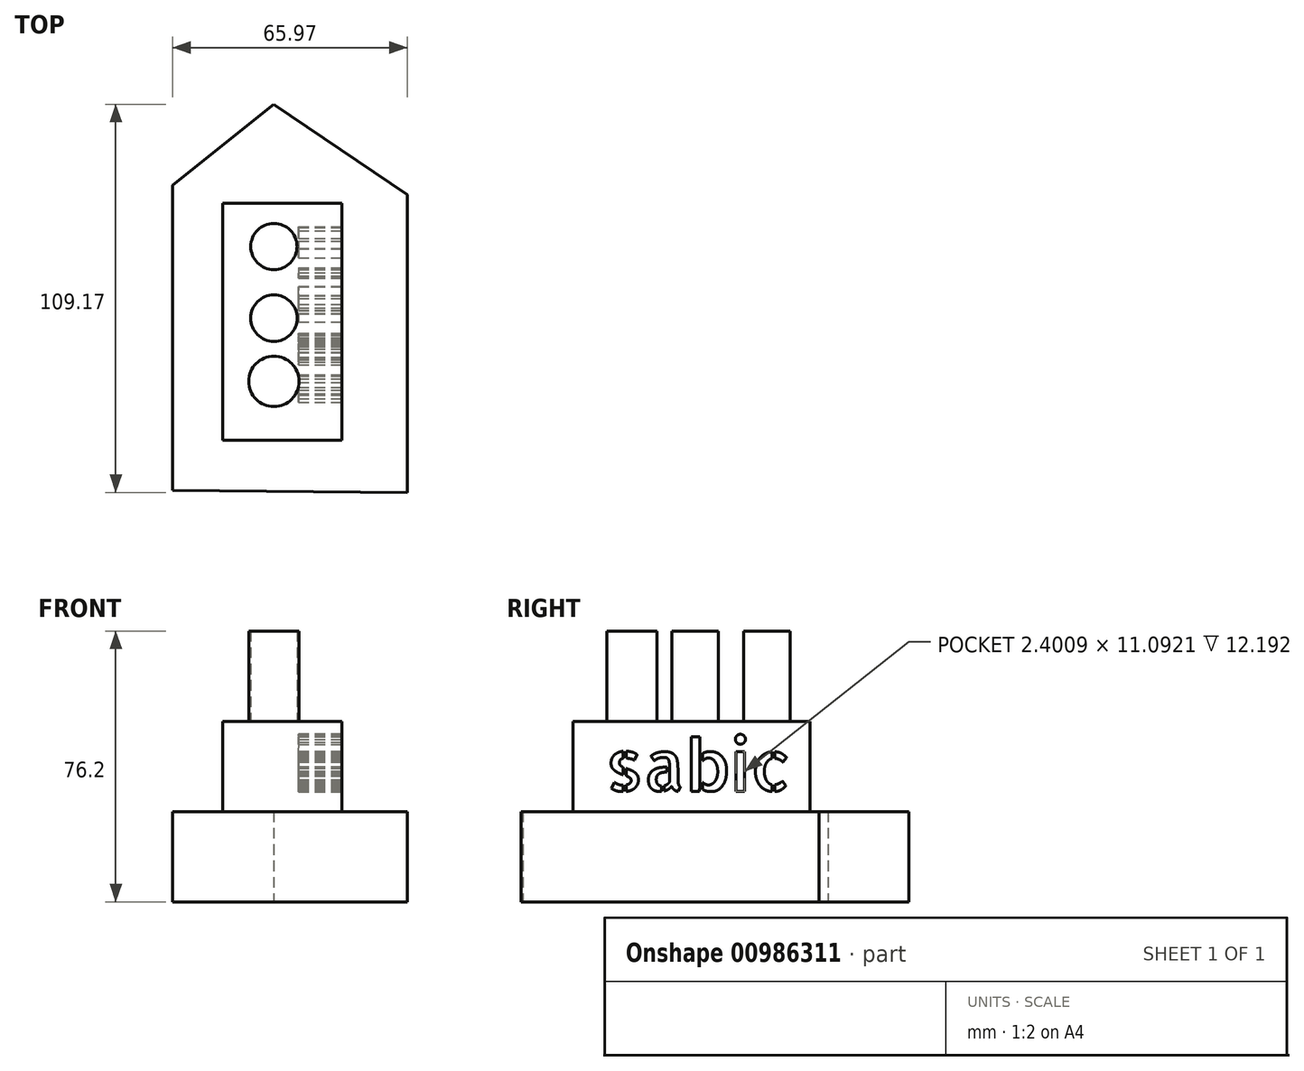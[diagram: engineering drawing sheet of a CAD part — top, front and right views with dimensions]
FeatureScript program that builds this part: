
annotation { "Feature Type Name" : "Feature", "Feature Type Description" : "" }
export const myFeature = defineFeature(function(context is Context, id is Id, definition is map)
    precondition{}
    {
        {
            var Q0;
            Q0=qCreatedBy(makeId("Top.planeOp"),FACE);
            var sketch = newSketch(context, id + "F0", { "sketchPlane" : qUnion([Q0])});
            skLineSegment(sketch, "E0", {"start": v(0, 50.39) * mm, "end": v(37.5, 25.01) * mm});
            skLineSegment(sketch, "E1", {"start": v(37.5, 25.01) * mm, "end": v(37.5, -58.78) * mm});
            skLineSegment(sketch, "E2", {"start": v(0, 50.39) * mm, "end": v(-28.46, 27.62) * mm});
            skLineSegment(sketch, "E3", {"start": v(-28.46, 27.62) * mm, "end": v(-28.46, -58.2) * mm});
            skLineSegment(sketch, "E4", {"start": v(-28.46, -58.2) * mm, "end": v(37.5, -58.78) * mm});
            skSolve(sketch);
        }
        {
            var Q0;
            Q0 = qSketchRegion(id + "F0", true);
            extrude(context, id + "F1", {"entities" : qUnion([Q0]), "depth" : 25.4 * mm, "offsetDistance" : 25.4 * mm});
        }
        {
            var Q0;
            Q0=makeQuery(id+"F1.opExtrude","CAP_FACE",FACE,{"disambiguationData":[OSD([sQuery(id+"F0.wireOp",EDGE,"E0"),sQuery(id+"F0.wireOp",EDGE,"E1"),sQuery(id+"F0.wireOp",EDGE,"E2"),sQuery(id+"F0.wireOp",EDGE,"E3"),sQuery(id+"F0.wireOp",EDGE,"E4")])],"isStart":false});
            var sketch = newSketch(context, id + "F2", { "sketchPlane" : qUnion([Q0])});
            skLineSegment(sketch, "E5.bottom", {"start": v(-14.38, 22.52) * mm, "end": v(19.07, 22.52) * mm});
            skLineSegment(sketch, "E5.top", {"start": v(-14.38, -44.1) * mm, "end": v(19.07, -44.1) * mm});
            skLineSegment(sketch, "E5.left", {"start": v(-14.38, 22.52) * mm, "end": v(-14.38, -44.1) * mm});
            skLineSegment(sketch, "E5.right", {"start": v(19.07, 22.52) * mm, "end": v(19.07, -44.1) * mm});
            skSolve(sketch);
        }
        {
            var Q0;
            Q0 = qSketchRegion(id + "F2", true);
            extrude(context, id + "F3", {"entities" : qUnion([Q0]), "operationType" : NewBodyOperationType.ADD, "depth" : 25.4 * mm, "offsetDistance" : 25.4 * mm});
        }
        {
            var Q0;
            Q0=makeQuery(id+"F3.opExtrude","SWEPT_FACE",FACE,{"disambiguationData":[OSD([sQuery(id+"F2.wireOp",EDGE,"E5.right")])]});
            var sketch = newSketch(context, id + "F4", { "sketchPlane" : qUnion([Q0])});
            skText(sketch, "E6", { "text": "sabic", "fontName": "AllertaStencil-Regular.ttf"});
            const initialGuessF4  = {"E6": [-0.03488, 0.0311, 1, 0, 0.0145]};
            skSetInitialGuess(sketch, initialGuessF4);
            skSolve(sketch);
        }
        {
            var Q0;
            Q0 = qSketchRegion(id + "F4", true);
            extrude(context, id + "F5", {"entities" : qUnion([Q0]), "operationType" : NewBodyOperationType.REMOVE, "endBound" : BoundingType.SYMMETRIC, "oppositeDirection" : true, "depth" : 24.38 * mm, "offsetDistance" : 25.4 * mm});
        }
        {
            var Q0;
            Q0=makeQuery(id+"F3.opExtrude","CAP_FACE",FACE,{"disambiguationData":[OSD([sQuery(id+"F2.wireOp",EDGE,"E5.bottom"),sQuery(id+"F2.wireOp",EDGE,"E5.top"),sQuery(id+"F2.wireOp",EDGE,"E5.left"),sQuery(id+"F2.wireOp",EDGE,"E5.right")])],"isStart":false});
            var sketch = newSketch(context, id + "F6", { "sketchPlane" : qUnion([Q0])});
            skCircle(sketch, "E7", {"center": v(0, 10.4) * mm, "radius": 6.5 * mm});
            skCircle(sketch, "E8", {"center": v(0, -9.74) * mm, "radius": 6.55 * mm});
            skCircle(sketch, "E9", {"center": v(0, -27.55) * mm, "radius": 7.08 * mm});
            skSolve(sketch);
        }
        {
            var Q0;
            Q0=makeQuery(id+"F6.imprint","IMPRINT",FACE,{"disambiguationData":[TD([[makeQuery(id+"F6.imprint","IMPRINT",EDGE,{"derivedFrom":sQuery(id+"F6.wireOp",EDGE,"E7")}),1.0]])]});
            var Q1;
            Q1=makeQuery(id+"F6.imprint","IMPRINT",FACE,{"disambiguationData":[TD([[makeQuery(id+"F6.imprint","IMPRINT",EDGE,{"derivedFrom":sQuery(id+"F6.wireOp",EDGE,"E8")}),1.0]])]});
            var Q2;
            Q2=makeQuery(id+"F6.imprint","IMPRINT",FACE,{"disambiguationData":[TD([[makeQuery(id+"F6.imprint","IMPRINT",EDGE,{"derivedFrom":sQuery(id+"F6.wireOp",EDGE,"E9")}),1.0]])]});
            extrude(context, id + "F7", {"entities" : qUnion([Q0, Q1, Q2]), "operationType" : NewBodyOperationType.ADD, "depth" : 25.4 * mm, "offsetDistance" : 25.4 * mm});
        }
    });
